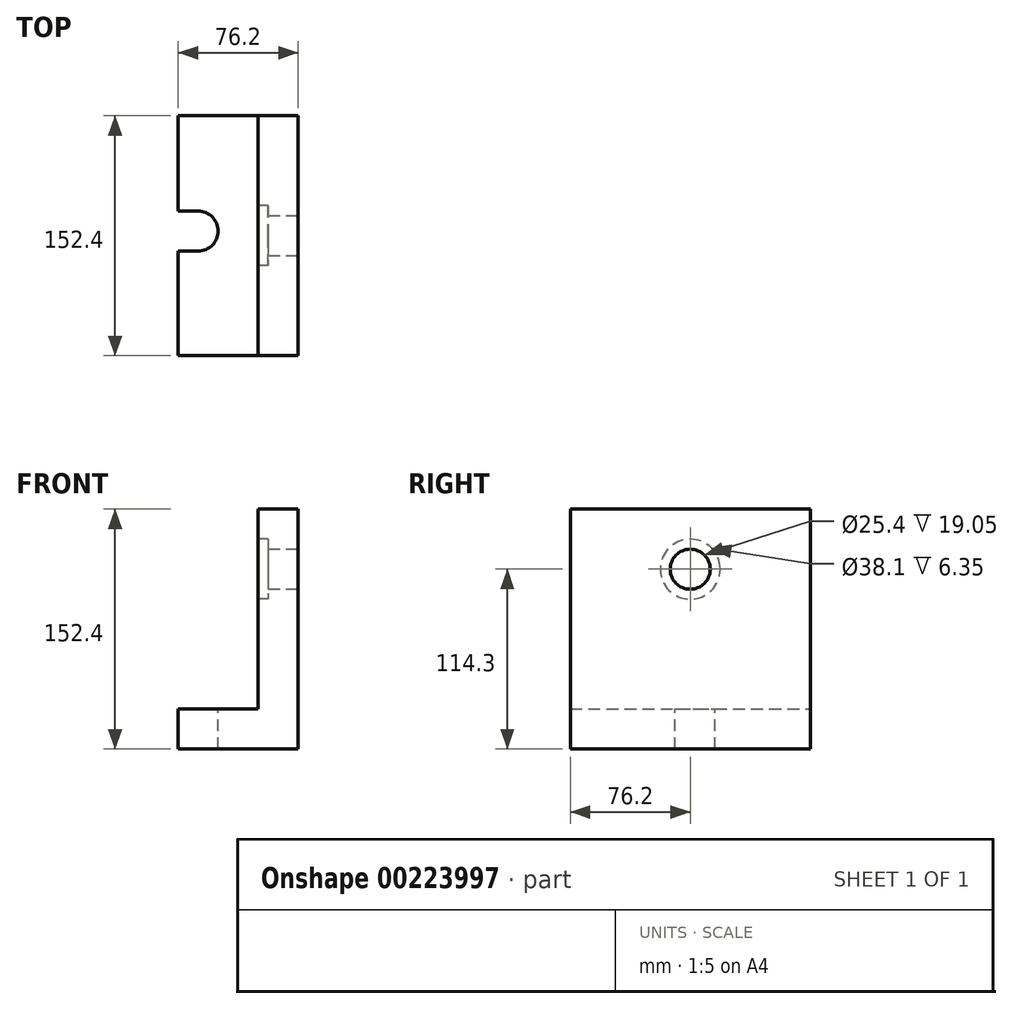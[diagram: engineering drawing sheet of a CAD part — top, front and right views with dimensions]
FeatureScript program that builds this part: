
annotation { "Feature Type Name" : "Feature", "Feature Type Description" : "" }
export const myFeature = defineFeature(function(context is Context, id is Id, definition is map)
    precondition{}
    {
        {
            var Q0;
            Q0=qCreatedBy(makeId("Front.planeOp"),FACE);
            var sketch = newSketch(context, id + "F0", { "sketchPlane" : qUnion([Q0])});
            skLineSegment(sketch, "E0", {"start": v(-25.4, 25.4) * mm, "end": v(-76.2, 25.4) * mm});
            skLineSegment(sketch, "E1", {"start": v(-76.2, 25.4) * mm, "end": v(-76.2, 0) * mm});
            skLineSegment(sketch, "E2", {"start": v(-76.2, 0) * mm, "end": v(0, 0) * mm});
            skLineSegment(sketch, "E3", {"start": v(0, 0) * mm, "end": v(0, 152.4) * mm});
            skLineSegment(sketch, "E4", {"start": v(-25.4, 25.4) * mm, "end": v(-25.4, 152.4) * mm});
            skLineSegment(sketch, "E5", {"start": v(-25.4, 152.4) * mm, "end": v(0, 152.4) * mm});
            skSolve(sketch);
        }
        {
            var Q0;
            Q0 = qSketchRegion(id + "F0", true);
            extrude(context, id + "F1", {"entities" : qUnion([Q0]), "endBound" : BoundingType.SYMMETRIC, "depth" : 152.4 * mm});
        }
        {
            var Q0;
            Q0=makeQuery(id+"F1.opExtrude","SWEPT_FACE",FACE,{"disambiguationData":[OSD([sQuery(id+"F0.wireOp",EDGE,"E3")])]});
            var sketch = newSketch(context, id + "F2", { "sketchPlane" : qUnion([Q0])});
            skCircle(sketch, "E6", {"center": v(0, 114.3) * mm, "radius": 12.7 * mm});
            skSolve(sketch);
        }
        {
            var Q0;
            Q0=makeQuery(id+"F2.imprint","IMPRINT",FACE,{"disambiguationData":[TD([[makeQuery(id+"F2.imprint","IMPRINT",EDGE,{"derivedFrom":sQuery(id+"F2.wireOp",EDGE,"E6")}),1.0]])]});
            extrude(context, id + "F3", {"entities" : qUnion([Q0]), "operationType" : NewBodyOperationType.REMOVE, "endBound" : BoundingType.THROUGH_ALL, "oppositeDirection" : true, "depth" : 25.4 * mm});
        }
        {
            var Q0;
            Q0=makeQuery(id+"F1.opExtrude","SWEPT_FACE",FACE,{"disambiguationData":[OSD([sQuery(id+"F0.wireOp",EDGE,"E0")])]});
            var sketch = newSketch(context, id + "F4", { "sketchPlane" : qUnion([Q0])});
            skPoint(sketch, "E7.middle", {"position": v(-76.2, 2.95) * mm});
            skLineSegment(sketch, "E8.bottom", {"start": v(-72.6, 7.93) * mm, "end": v(-75.03, 7.93) * mm});
            skLineSegment(sketch, "E9", {"start": v(-76.2, 2.95) * mm, "end": v(-76.2, 15.65) * mm});
            skLineSegment(sketch, "E10", {"start": v(-76.2, 2.95) * mm, "end": v(-76.2, -9.75) * mm});
            skLineSegment(sketch, "E11", {"start": v(-76.2, -9.75) * mm, "end": v(-63.5, -9.75) * mm});
            skLineSegment(sketch, "E12", {"start": v(-76.2, 15.65) * mm, "end": v(-63.5, 15.65) * mm});
            skArc(sketch, "E13", {"start": v(-63.5, 15.65) * mm, "mid": v(-50.8, 2.95) * mm, "end": v(-63.5, -9.75) * mm});
            skSolve(sketch);
        }
        {
            var Q0;
            Q0=makeQuery(id+"F4.imprint","IMPRINT",FACE,{"disambiguationData":[TD([[makeQuery(id+"F4.imprint","IMPRINT",EDGE,{"derivedFrom":sQuery(id+"F4.wireOp",EDGE,"E9")}),-1.0]])]});
            extrude(context, id + "F5", {"entities" : qUnion([Q0]), "operationType" : NewBodyOperationType.REMOVE, "oppositeDirection" : true, "depth" : 50.8 * mm});
        }
        {
            var Q0;
            Q0=makeQuery(id+"F1.opExtrude","SWEPT_FACE",FACE,{"disambiguationData":[OSD([sQuery(id+"F0.wireOp",EDGE,"E4")])]});
            var sketch = newSketch(context, id + "F6", { "sketchPlane" : qUnion([Q0])});
            skCircle(sketch, "E14", {"center": v(0, 114.3) * mm, "radius": 19.05 * mm});
            skSolve(sketch);
        }
        {
            var Q0;
            Q0=makeQuery(id+"F6.imprint","IMPRINT",FACE,{"disambiguationData":[TD([[makeQuery(id+"F6.imprint","IMPRINT",EDGE,{"derivedFrom":sQuery(id+"F6.wireOp",EDGE,"E14")}),1.0]])]});
            var Q1;
            Q1=sQuery(id+"F6.wireOp",EDGE,"E14");
            extrude(context, id + "F7", {"entities" : qUnion([Q0]), "operationType" : NewBodyOperationType.REMOVE, "surfaceEntities" : qUnion([Q1]), "oppositeDirection" : true, "depth" : 6.35 * mm});
        }
    });
